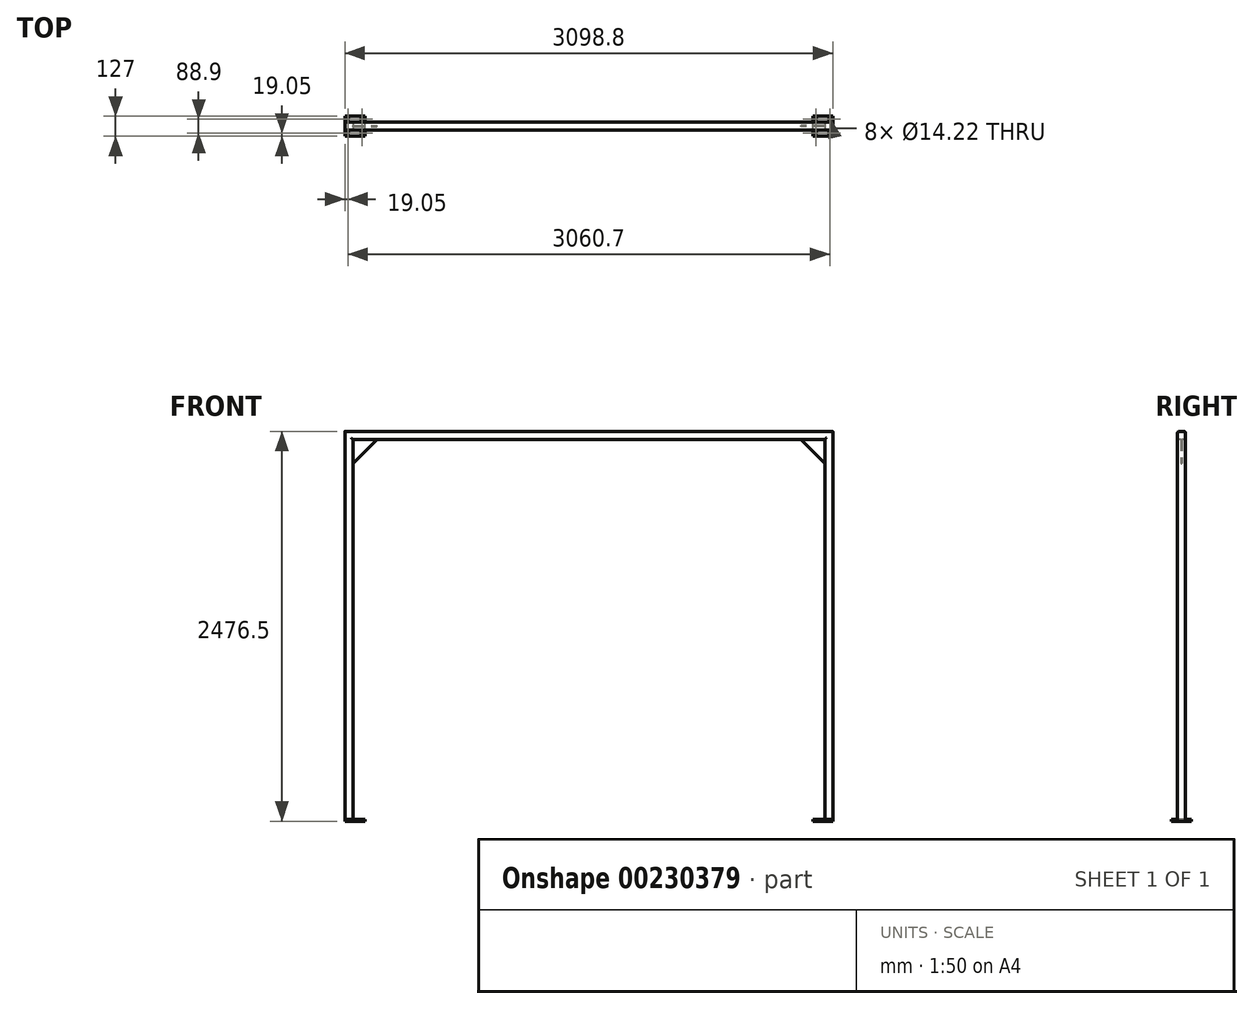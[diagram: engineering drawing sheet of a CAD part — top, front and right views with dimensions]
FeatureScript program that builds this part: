
annotation { "Feature Type Name" : "Feature", "Feature Type Description" : "" }
export const myFeature = defineFeature(function(context is Context, id is Id, definition is map)
    precondition{}
    {
        {
            var Q0;
            Q0=qCreatedBy(makeId("Front.planeOp"),FACE);
            var sketch = newSketch(context, id + "F0", { "sketchPlane" : qUnion([Q0])});
            skLineSegment(sketch, "E0", {"start": v(0, 0) * mm, "end": v(0, 2438.4) * mm});
            skLineSegment(sketch, "E1", {"start": v(0, 2438.4) * mm, "end": v(3048, 2438.4) * mm});
            skLineSegment(sketch, "E2", {"start": v(3048, 2438.4) * mm, "end": v(3048, 0) * mm});
            skSolve(sketch);
        }
        {
            var Q0;
            Q0=qCreatedBy(makeId("Top.planeOp"),FACE);
            var sketch = newSketch(context, id + "F1", { "sketchPlane" : qUnion([Q0])});
            skLineSegment(sketch, "E3.bottom", {"start": v(-15.88, 25.4) * mm, "end": v(15.88, 25.4) * mm});
            skLineSegment(sketch, "E3.top", {"start": v(-15.88, -25.4) * mm, "end": v(15.88, -25.4) * mm});
            skLineSegment(sketch, "E3.left", {"start": v(-25.4, 15.88) * mm, "end": v(-25.4, -15.87) * mm});
            skLineSegment(sketch, "E3.right", {"start": v(25.4, 15.88) * mm, "end": v(25.4, -15.88) * mm});
            skPoint(sketch, "E3.middle", {"position": v(0, 0) * mm});
            skPoint(sketch, "E4.visualSharp", {"position": v(-25.4, 25.4) * mm});
            skArc(sketch, "E4.filletArc", {"start": v(-15.88, 25.4) * mm, "mid": v(-22.61, 22.61) * mm, "end": v(-25.4, 15.88) * mm});
            skPoint(sketch, "E5.visualSharp", {"position": v(-25.4, -25.4) * mm});
            skArc(sketch, "E5.filletArc", {"start": v(-25.4, -15.87) * mm, "mid": v(-22.61, -22.61) * mm, "end": v(-15.88, -25.4) * mm});
            skPoint(sketch, "E6.visualSharp", {"position": v(25.4, 25.4) * mm});
            skArc(sketch, "E6.filletArc", {"start": v(25.4, 15.88) * mm, "mid": v(22.61, 22.61) * mm, "end": v(15.88, 25.4) * mm});
            skPoint(sketch, "E7.visualSharp", {"position": v(25.4, -25.4) * mm});
            skArc(sketch, "E7.filletArc", {"start": v(15.88, -25.4) * mm, "mid": v(22.61, -22.61) * mm, "end": v(25.4, -15.88) * mm});
            skSolve(sketch);
        }
        {
            var Q0;
            Q0=makeQuery(id+"F1.imprint","IMPRINT",FACE,{"disambiguationData":[TD([[makeQuery(id+"F1.imprint","IMPRINT",EDGE,{"derivedFrom":sQuery(id+"F1.wireOp",EDGE,"E3.bottom")}),-1.0]])]});
            var Q1;
            Q1=sQuery(id+"F0.wireOp",EDGE,"E0");
            var Q2;
            Q2=sQuery(id+"F0.wireOp",EDGE,"E1");
            var Q3;
            Q3=sQuery(id+"F0.wireOp",EDGE,"E2");
            sweep(context, id + "F2", {"profiles" : qUnion([Q0]), "path" : qUnion([Q1, Q2, Q3])});
        }
        {
            var Q0;
            Q0=qCreatedBy(makeId("Top.planeOp"),FACE);
            var sketch = newSketch(context, id + "F3", { "sketchPlane" : qUnion([Q0])});
            skLineSegment(sketch, "E8.0", {"start": v(-25.4, 15.88) * mm, "end": v(-25.4, -15.87) * mm, "construction": true});
            skLineSegment(sketch, "E9", {"start": v(-25.4, 0) * mm, "end": v(38.1, 0) * mm, "construction": true});
            skLineSegment(sketch, "E10.bottom", {"start": v(-25.4, -63.5) * mm, "end": v(101.6, -63.5) * mm});
            skLineSegment(sketch, "E10.top", {"start": v(-25.4, 63.5) * mm, "end": v(101.6, 63.5) * mm});
            skLineSegment(sketch, "E10.left", {"start": v(-25.4, -63.5) * mm, "end": v(-25.4, 63.5) * mm});
            skLineSegment(sketch, "E10.right", {"start": v(101.6, -63.5) * mm, "end": v(101.6, 63.5) * mm});
            skPoint(sketch, "E10.middle", {"position": v(38.1, 0) * mm});
            skLineSegment(sketch, "E11.0", {"start": v(-6.35, -44.45) * mm, "end": v(82.55, -44.45) * mm, "construction": true});
            skLineSegment(sketch, "E11.1", {"start": v(-6.35, -44.45) * mm, "end": v(-6.35, 44.45) * mm, "construction": true});
            skLineSegment(sketch, "E11.2", {"start": v(-6.35, 44.45) * mm, "end": v(82.55, 44.45) * mm, "construction": true});
            skLineSegment(sketch, "E11.3", {"start": v(82.55, -44.45) * mm, "end": v(82.55, 44.45) * mm, "construction": true});
            skCircle(sketch, "E12", {"center": v(-6.35, -44.45) * mm, "radius": 7.11 * mm});
            skCircle(sketch, "E13.0.1.0", {"center": v(-6.35, 44.45) * mm, "radius": 7.11 * mm});
            skCircle(sketch, "E13.1.0.0", {"center": v(82.55, -44.45) * mm, "radius": 7.11 * mm});
            skCircle(sketch, "E13.1.1.0", {"center": v(82.55, 44.45) * mm, "radius": 7.11 * mm});
            skLineSegment(sketch, "E14.1.0.0", {"start": v(2946.4, 63.5) * mm, "end": v(3073.4, 63.5) * mm});
            skLineSegment(sketch, "E14.1.0.1", {"start": v(3073.4, -63.5) * mm, "end": v(3073.4, 63.5) * mm});
            skLineSegment(sketch, "E14.1.0.2", {"start": v(3054.35, -44.45) * mm, "end": v(3054.35, 44.45) * mm, "construction": true});
            skPoint(sketch, "E14.1.0.3", {"position": v(3009.9, 0) * mm});
            skLineSegment(sketch, "E14.1.0.4", {"start": v(2946.4, -63.5) * mm, "end": v(3073.4, -63.5) * mm});
            skLineSegment(sketch, "E14.1.0.5", {"start": v(2965.45, 44.45) * mm, "end": v(3054.35, 44.45) * mm, "construction": true});
            skLineSegment(sketch, "E14.1.0.6", {"start": v(2965.45, -44.45) * mm, "end": v(3054.35, -44.45) * mm, "construction": true});
            skLineSegment(sketch, "E14.1.0.7", {"start": v(2946.4, 0) * mm, "end": v(3009.9, 0) * mm, "construction": true});
            skLineSegment(sketch, "E14.1.0.8", {"start": v(2965.45, -44.45) * mm, "end": v(3054.35, -44.45) * mm, "construction": true});
            skLineSegment(sketch, "E14.1.0.9", {"start": v(2946.4, 15.88) * mm, "end": v(2946.4, -15.87) * mm, "construction": true});
            skCircle(sketch, "E14.1.0.10", {"center": v(3054.35, 44.45) * mm, "radius": 7.11 * mm});
            skLineSegment(sketch, "E14.1.0.11", {"start": v(2965.45, -44.45) * mm, "end": v(2965.45, 44.45) * mm, "construction": true});
            skLineSegment(sketch, "E14.1.0.12", {"start": v(2946.4, -63.5) * mm, "end": v(2946.4, 63.5) * mm});
            skLineSegment(sketch, "E14.1.0.13", {"start": v(2965.45, -44.45) * mm, "end": v(2965.45, 44.45) * mm, "construction": true});
            skCircle(sketch, "E14.1.0.14", {"center": v(2965.45, 44.45) * mm, "radius": 7.11 * mm});
            skCircle(sketch, "E14.1.0.15", {"center": v(3054.35, -44.45) * mm, "radius": 7.11 * mm});
            skCircle(sketch, "E14.1.0.16", {"center": v(2965.45, -44.45) * mm, "radius": 7.11 * mm});
            skLineSegment(sketch, "E14.direction1", {"start": v(-25.4, -63.5) * mm, "end": v(2946.4, -63.5) * mm, "construction": true});
            skSolve(sketch);
        }
        {
            var Q0;
            Q0 = qSketchRegion(id + "F3", true);
            extrude(context, id + "F4", {"entities" : qUnion([Q0]), "operationType" : NewBodyOperationType.ADD, "oppositeDirection" : true, "depth" : 12.7 * mm});
        }
        {
            var Q0;
            Q0=qCreatedBy(makeId("Front.planeOp"),FACE);
            var sketch = newSketch(context, id + "F5", { "sketchPlane" : qUnion([Q0])});
            skLineSegment(sketch, "E15.0", {"start": v(25.4, 2413) * mm, "end": v(3022.6, 2413) * mm, "construction": true});
            skLineSegment(sketch, "E16.0", {"start": v(25.4, 0) * mm, "end": v(25.4, 2413) * mm, "construction": true});
            skLineSegment(sketch, "E17.0", {"start": v(3022.6, 2413) * mm, "end": v(3022.6, 0) * mm, "construction": true});
            skLineSegment(sketch, "E18.bottom", {"start": v(25.4, 2413) * mm, "end": v(177.8, 2413) * mm});
            skLineSegment(sketch, "E18.top", {"start": v(25.4, 2260.6) * mm, "end": v(177.8, 2260.6) * mm});
            skLineSegment(sketch, "E18.left", {"start": v(25.4, 2413) * mm, "end": v(25.4, 2260.6) * mm});
            skLineSegment(sketch, "E19", {"start": v(25.4, 2260.6) * mm, "end": v(177.8, 2413) * mm});
            skLineSegment(sketch, "E20", {"start": v(1524, 2413) * mm, "end": v(1524, 1962.66) * mm, "construction": true});
            skLineSegment(sketch, "E21.MirrorCS", {"start": v(3022.6, 2413) * mm, "end": v(2870.2, 2413) * mm});
            skLineSegment(sketch, "E22.MirrorCS", {"start": v(3022.6, 2260.6) * mm, "end": v(2870.2, 2260.6) * mm});
            skLineSegment(sketch, "E23.MirrorCS", {"start": v(3022.6, 2260.6) * mm, "end": v(2870.2, 2413) * mm});
            skLineSegment(sketch, "E24.MirrorCS", {"start": v(3022.6, 2413) * mm, "end": v(3022.6, 2260.6) * mm});
            skSolve(sketch);
        }
        {
            var Q0;
            Q0=makeQuery(id+"F5.imprint","IMPRINT",FACE,{"disambiguationData":[TD([[makeQuery(id+"F5.imprint","IMPRINT",EDGE,{"derivedFrom":sQuery(id+"F5.wireOp",EDGE,"E18.bottom")}),-1.0]])]});
            var Q1;
            Q1=makeQuery(id+"F5.imprint","IMPRINT",FACE,{"disambiguationData":[TD([[makeQuery(id+"F5.imprint","IMPRINT",EDGE,{"derivedFrom":sQuery(id+"F5.wireOp",EDGE,"E21.MirrorCS")}),1.0]])]});
            extrude(context, id + "F6", {"entities" : qUnion([Q0, Q1]), "operationType" : NewBodyOperationType.ADD, "endBound" : BoundingType.SYMMETRIC, "depth" : 6.35 * mm});
        }
    });
